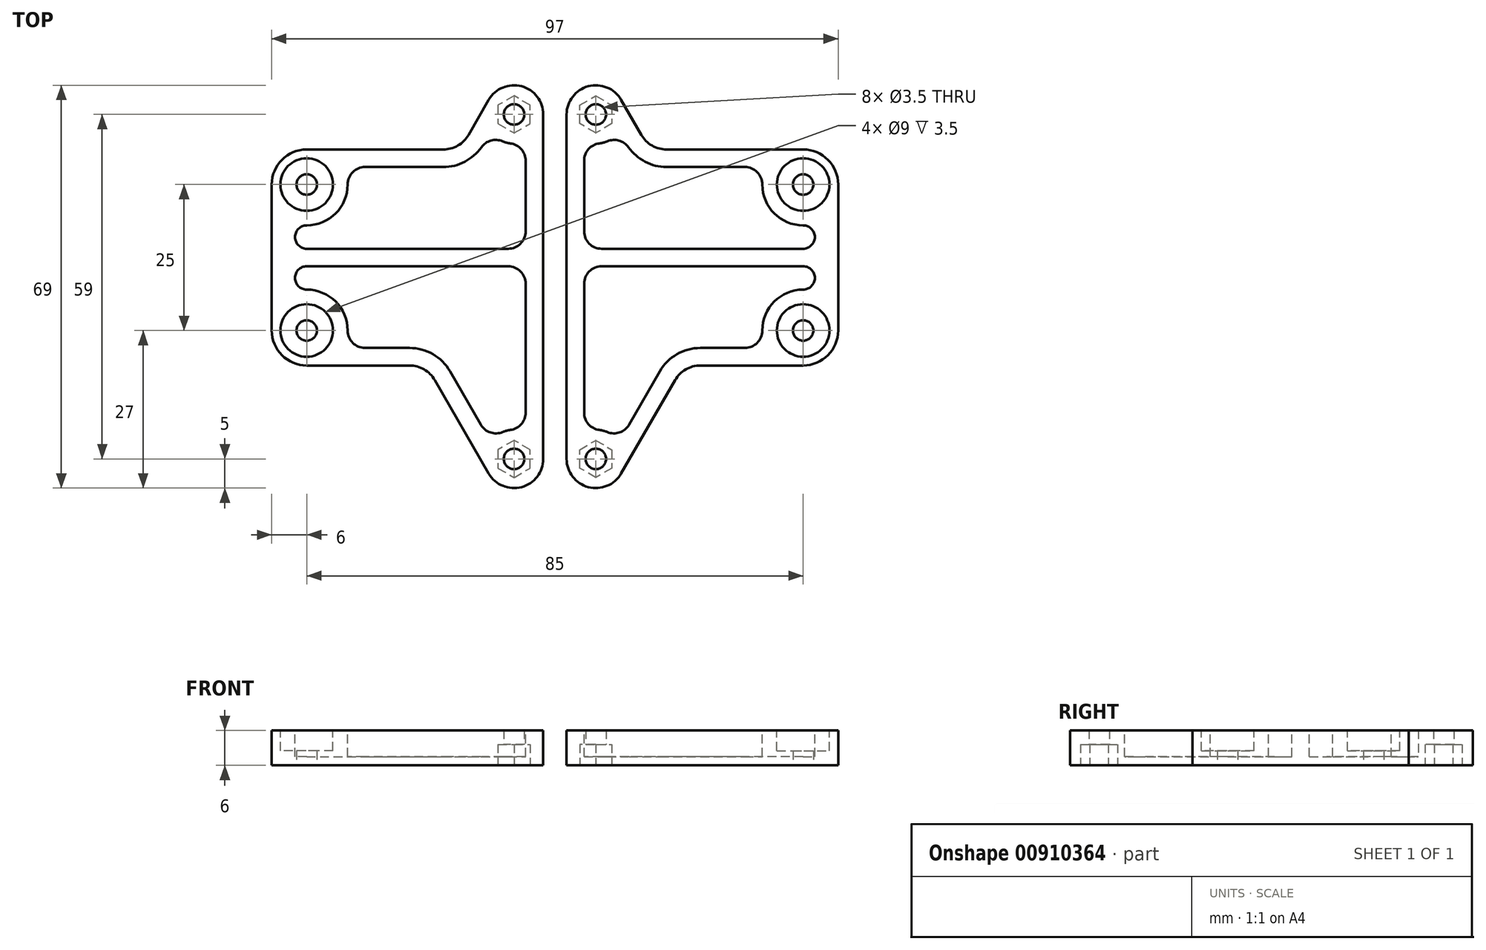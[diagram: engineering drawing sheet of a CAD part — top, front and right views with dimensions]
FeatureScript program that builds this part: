
annotation { "Feature Type Name" : "Feature", "Feature Type Description" : "" }
export const myFeature = defineFeature(function(context is Context, id is Id, definition is map)
    precondition{}
    {
        {
            var Q0;
            Q0=qCreatedBy(makeId("Top.planeOp"),FACE);
            var sketch = newSketch(context, id + "F0", { "sketchPlane" : qUnion([Q0])});
            skLineSegment(sketch, "E0", {"start": v(-42.5, 18.5) * mm, "end": v(-19.12, 18.5) * mm});
            skLineSegment(sketch, "E1", {"start": v(-2, 24.5) * mm, "end": v(-2, -34.5) * mm});
            skLineSegment(sketch, "E2", {"start": v(-24.9, -18.5) * mm, "end": v(-42.5, -18.5) * mm});
            skCircle(sketch, "E3", {"center": v(-42.5, 12.5) * mm, "radius": 1.75 * mm});
            skCircle(sketch, "E4", {"center": v(-42.5, -12.5) * mm, "radius": 1.75 * mm});
            skCircle(sketch, "E5", {"center": v(-7, 24.5) * mm, "radius": 1.75 * mm});
            skCircle(sketch, "E6", {"center": v(-7, -34.5) * mm, "radius": 1.75 * mm});
            skLineSegment(sketch, "E7", {"start": v(0, 32.5) * mm, "end": v(-48.5, 32.5) * mm, "construction": true});
            skArc(sketch, "E8", {"start": v(-2, 24.5) * mm, "mid": v(-5.7, 29.33) * mm, "end": v(-11.33, 27) * mm});
            skArc(sketch, "E9", {"start": v(-2, -34.5) * mm, "mid": v(-5.7, -39.33) * mm, "end": v(-11.33, -37) * mm});
            skLineSegment(sketch, "E10", {"start": v(-11.33, -37) * mm, "end": v(-20.57, -21) * mm});
            skLineSegment(sketch, "E11", {"start": v(-11.33, 27) * mm, "end": v(-14.8, 21) * mm});
            skArc(sketch, "E12", {"start": v(-42.5, 18.5) * mm, "mid": v(-46.74, 16.74) * mm, "end": v(-48.5, 12.5) * mm});
            skArc(sketch, "E13", {"start": v(-42.5, -18.5) * mm, "mid": v(-46.74, -16.74) * mm, "end": v(-48.5, -12.5) * mm});
            skLineSegment(sketch, "E14", {"start": v(-48.5, -12.5) * mm, "end": v(-48.5, 12.5) * mm});
            skPoint(sketch, "E15.visualSharp", {"position": v(-16.24, 18.5) * mm});
            skArc(sketch, "E15.filletArc", {"start": v(-19.12, 18.5) * mm, "mid": v(-16.62, 19.17) * mm, "end": v(-14.8, 21) * mm});
            skPoint(sketch, "E16.visualSharp", {"position": v(-22.01, -18.5) * mm});
            skArc(sketch, "E16.filletArc", {"start": v(-20.57, -21) * mm, "mid": v(-22.4, -19.17) * mm, "end": v(-24.9, -18.5) * mm});
            skLineSegment(sketch, "E17.bottom", {"start": v(-11, 28.5) * mm, "end": v(77, 28.5) * mm, "construction": true});
            skLineSegment(sketch, "E17.top", {"start": v(-11, -38.5) * mm, "end": v(77, -38.5) * mm, "construction": true});
            skLineSegment(sketch, "E17.left", {"start": v(-11, 28.5) * mm, "end": v(-11, -38.5) * mm, "construction": true});
            skLineSegment(sketch, "E17.right", {"start": v(77, 28.5) * mm, "end": v(77, -38.5) * mm, "construction": true});
            skCircle(sketch, "E18", {"center": v(-42.5, -12.5) * mm, "radius": 4 * mm, "construction": true});
            skSolve(sketch);
        }
        {
            var Q0;
            Q0 = qSketchRegion(id + "F0", true);
            extrude(context, id + "F1", {"entities" : qUnion([Q0]), "depth" : 6 * mm, "offsetDistance" : 25.4 * mm});
        }
        {
            var Q0;
            Q0=makeQuery(id+"F1.opExtrude","CAP_FACE",FACE,{"disambiguationData":[OSD([sQuery(id+"F0.wireOp",EDGE,"E0"),sQuery(id+"F0.wireOp",EDGE,"E1"),sQuery(id+"F0.wireOp",EDGE,"E2"),sQuery(id+"F0.wireOp",EDGE,"E3"),sQuery(id+"F0.wireOp",EDGE,"E4"),sQuery(id+"F0.wireOp",EDGE,"E5"),sQuery(id+"F0.wireOp",EDGE,"E6"),sQuery(id+"F0.wireOp",EDGE,"E8"),sQuery(id+"F0.wireOp",EDGE,"E9"),sQuery(id+"F0.wireOp",EDGE,"E10"),sQuery(id+"F0.wireOp",EDGE,"E11"),sQuery(id+"F0.wireOp",EDGE,"E12"),sQuery(id+"F0.wireOp",EDGE,"E13"),sQuery(id+"F0.wireOp",EDGE,"E14"),sQuery(id+"F0.wireOp",EDGE,"E15.filletArc"),sQuery(id+"F0.wireOp",EDGE,"E16.filletArc")])],"isStart":false});
            var sketch = newSketch(context, id + "F2", { "sketchPlane" : qUnion([Q0])});
            skCircle(sketch, "E19", {"center": v(-42.5, 12.5) * mm, "radius": 4.5 * mm});
            skCircle(sketch, "E20", {"center": v(-42.5, -12.5) * mm, "radius": 4.5 * mm});
            skSolve(sketch);
        }
        {
            var Q0;
            Q0 = qSketchRegion(id + "F2", true);
            var Q1;
            Q1=makeQuery(id+"F1.opExtrude","CAP_FACE",FACE,{"disambiguationData":[OSD([sQuery(id+"F0.wireOp",EDGE,"E0"),sQuery(id+"F0.wireOp",EDGE,"E1"),sQuery(id+"F0.wireOp",EDGE,"E2"),sQuery(id+"F0.wireOp",EDGE,"E3"),sQuery(id+"F0.wireOp",EDGE,"E4"),sQuery(id+"F0.wireOp",EDGE,"E5"),sQuery(id+"F0.wireOp",EDGE,"E6"),sQuery(id+"F0.wireOp",EDGE,"E8"),sQuery(id+"F0.wireOp",EDGE,"E9"),sQuery(id+"F0.wireOp",EDGE,"E10"),sQuery(id+"F0.wireOp",EDGE,"E11"),sQuery(id+"F0.wireOp",EDGE,"E12"),sQuery(id+"F0.wireOp",EDGE,"E13"),sQuery(id+"F0.wireOp",EDGE,"E14"),sQuery(id+"F0.wireOp",EDGE,"E15.filletArc"),sQuery(id+"F0.wireOp",EDGE,"E16.filletArc")])],"isStart":true});
            extrude(context, id + "F3", {"entities" : qUnion([Q0]), "operationType" : NewBodyOperationType.REMOVE, "endBound" : BoundingType.UP_TO_SURFACE, "oppositeDirection" : true, "depth" : 25.4 * mm, "endBoundEntityFace" : qUnion([Q1]), "hasOffset" : true, "offsetDistance" : 2.5 * mm});
        }
        {
            var Q0;
            Q0=makeQuery(id+"F1.opExtrude","CAP_FACE",FACE,{"disambiguationData":[OSD([sQuery(id+"F0.wireOp",EDGE,"E0"),sQuery(id+"F0.wireOp",EDGE,"E1"),sQuery(id+"F0.wireOp",EDGE,"E2"),sQuery(id+"F0.wireOp",EDGE,"E3"),sQuery(id+"F0.wireOp",EDGE,"E4"),sQuery(id+"F0.wireOp",EDGE,"E5"),sQuery(id+"F0.wireOp",EDGE,"E6"),sQuery(id+"F0.wireOp",EDGE,"E8"),sQuery(id+"F0.wireOp",EDGE,"E9"),sQuery(id+"F0.wireOp",EDGE,"E10"),sQuery(id+"F0.wireOp",EDGE,"E11"),sQuery(id+"F0.wireOp",EDGE,"E12"),sQuery(id+"F0.wireOp",EDGE,"E13"),sQuery(id+"F0.wireOp",EDGE,"E14"),sQuery(id+"F0.wireOp",EDGE,"E15.filletArc"),sQuery(id+"F0.wireOp",EDGE,"E16.filletArc")])],"isStart":true});
            var sketch = newSketch(context, id + "F4", { "sketchPlane" : qUnion([Q0])});
            skCircle(sketch, "E21.cCircle", {"center": v(-7, 34.5) * mm, "radius": 2.75 * mm, "construction": true});
            skLineSegment(sketch, "E21.0", {"start": v(-4.25, 36.09) * mm, "end": v(-4.25, 32.91) * mm});
            skLineSegment(sketch, "E21.1", {"start": v(-4.25, 32.91) * mm, "end": v(-7, 31.32) * mm});
            skLineSegment(sketch, "E21.2", {"start": v(-7, 31.32) * mm, "end": v(-9.75, 32.91) * mm});
            skLineSegment(sketch, "E21.3", {"start": v(-9.75, 32.91) * mm, "end": v(-9.75, 36.09) * mm});
            skLineSegment(sketch, "E21.4", {"start": v(-9.75, 36.09) * mm, "end": v(-7, 37.68) * mm});
            skLineSegment(sketch, "E21.5", {"start": v(-7, 37.68) * mm, "end": v(-4.25, 36.09) * mm});
            skPoint(sketch, "E21.0.midPoint", {"position": v(-4.25, 34.5) * mm});
            skCircle(sketch, "E22.cCircle", {"center": v(-7, -24.5) * mm, "radius": 2.75 * mm, "construction": true});
            skLineSegment(sketch, "E22.0", {"start": v(-7, -21.32) * mm, "end": v(-4.25, -22.91) * mm});
            skLineSegment(sketch, "E22.1", {"start": v(-4.25, -22.91) * mm, "end": v(-4.25, -26.09) * mm});
            skLineSegment(sketch, "E22.2", {"start": v(-4.25, -26.09) * mm, "end": v(-7, -27.68) * mm});
            skLineSegment(sketch, "E22.3", {"start": v(-7, -27.68) * mm, "end": v(-9.75, -26.09) * mm});
            skLineSegment(sketch, "E22.4", {"start": v(-9.75, -26.09) * mm, "end": v(-9.75, -22.91) * mm});
            skLineSegment(sketch, "E22.5", {"start": v(-9.75, -22.91) * mm, "end": v(-7, -21.32) * mm});
            skPoint(sketch, "E22.0.midPoint", {"position": v(-5.63, -22.12) * mm});
            skSolve(sketch);
        }
        {
            var Q0;
            Q0 = qSketchRegion(id + "F4", true);
            var Q1;
            Q1=makeQuery(id+"F1.opExtrude","CAP_FACE",FACE,{"disambiguationData":[OSD([sQuery(id+"F0.wireOp",EDGE,"E0"),sQuery(id+"F0.wireOp",EDGE,"E1"),sQuery(id+"F0.wireOp",EDGE,"E2"),sQuery(id+"F0.wireOp",EDGE,"E3"),sQuery(id+"F0.wireOp",EDGE,"E4"),sQuery(id+"F0.wireOp",EDGE,"E5"),sQuery(id+"F0.wireOp",EDGE,"E6"),sQuery(id+"F0.wireOp",EDGE,"E8"),sQuery(id+"F0.wireOp",EDGE,"E9"),sQuery(id+"F0.wireOp",EDGE,"E10"),sQuery(id+"F0.wireOp",EDGE,"E11"),sQuery(id+"F0.wireOp",EDGE,"E12"),sQuery(id+"F0.wireOp",EDGE,"E13"),sQuery(id+"F0.wireOp",EDGE,"E14"),sQuery(id+"F0.wireOp",EDGE,"E15.filletArc"),sQuery(id+"F0.wireOp",EDGE,"E16.filletArc")])],"isStart":false});
            extrude(context, id + "F5", {"entities" : qUnion([Q0]), "operationType" : NewBodyOperationType.REMOVE, "endBound" : BoundingType.UP_TO_SURFACE, "oppositeDirection" : true, "depth" : 25.4 * mm, "endBoundEntityFace" : qUnion([Q1]), "hasOffset" : true, "offsetDistance" : 2.4 * mm});
        }
        {
            var Q0;
            Q0=makeQuery(id+"F1.opExtrude","CAP_FACE",FACE,{"disambiguationData":[OSD([sQuery(id+"F0.wireOp",EDGE,"E0"),sQuery(id+"F0.wireOp",EDGE,"E1"),sQuery(id+"F0.wireOp",EDGE,"E2"),sQuery(id+"F0.wireOp",EDGE,"E3"),sQuery(id+"F0.wireOp",EDGE,"E4"),sQuery(id+"F0.wireOp",EDGE,"E5"),sQuery(id+"F0.wireOp",EDGE,"E6"),sQuery(id+"F0.wireOp",EDGE,"E8"),sQuery(id+"F0.wireOp",EDGE,"E9"),sQuery(id+"F0.wireOp",EDGE,"E10"),sQuery(id+"F0.wireOp",EDGE,"E11"),sQuery(id+"F0.wireOp",EDGE,"E12"),sQuery(id+"F0.wireOp",EDGE,"E13"),sQuery(id+"F0.wireOp",EDGE,"E14"),sQuery(id+"F0.wireOp",EDGE,"E15.filletArc"),sQuery(id+"F0.wireOp",EDGE,"E16.filletArc")])],"isStart":false});
            var sketch = newSketch(context, id + "F6", { "sketchPlane" : qUnion([Q0])});
            skArc(sketch, "E23.0", {"start": v(-24.9, -15.5) * mm, "mid": v(-20.9, -16.57) * mm, "end": v(-17.97, -19.5) * mm});
            skLineSegment(sketch, "E23.1", {"start": v(-36.18, -15.5) * mm, "end": v(-24.9, -15.5) * mm});
            skLineSegment(sketch, "E23.2", {"start": v(-17.97, -19.5) * mm, "end": v(-11.02, -31.53) * mm});
            skLineSegment(sketch, "E23.4", {"start": v(-5, -29.92) * mm, "end": v(-5, -1.5) * mm});
            skLineSegment(sketch, "E23.5", {"start": v(-11.02, 21.53) * mm, "end": v(-12.2, 19.5) * mm});
            skArc(sketch, "E23.6", {"start": v(-12.2, 19.5) * mm, "mid": v(-15.12, 16.57) * mm, "end": v(-19.12, 15.5) * mm});
            skLineSegment(sketch, "E23.7", {"start": v(-19.12, 15.5) * mm, "end": v(-36.18, 15.5) * mm});
            skArc(sketch, "E24", {"start": v(-36.18, -15.5) * mm, "mid": v(-36.58, -8.76) * mm, "end": v(-42.5, -5.5) * mm});
            skArc(sketch, "E25", {"start": v(-42.5, 5.5) * mm, "mid": v(-36.58, 8.76) * mm, "end": v(-36.18, 15.5) * mm});
            skArc(sketch, "E26", {"start": v(-5, 19.92) * mm, "mid": v(-8.3, 19.67) * mm, "end": v(-11.02, 21.53) * mm});
            skArc(sketch, "E27", {"start": v(-5, -29.92) * mm, "mid": v(-8.3, -29.67) * mm, "end": v(-11.02, -31.53) * mm});
            skLineSegment(sketch, "E28", {"start": v(-5, 1.5) * mm, "end": v(-42.5, 1.5) * mm});
            skPoint(sketch, "E28.endSnap0", {"position": v(-42.5, 0) * mm});
            skLineSegment(sketch, "E29", {"start": v(-5, -1.5) * mm, "end": v(-42.5, -1.5) * mm});
            skLineSegment(sketch, "E30.trimOffspring", {"start": v(-5, 1.5) * mm, "end": v(-5, 19.92) * mm});
            skArc(sketch, "E31", {"start": v(-42.5, 5.5) * mm, "mid": v(-44.5, 3.5) * mm, "end": v(-42.5, 1.5) * mm});
            skArc(sketch, "E32", {"start": v(-42.5, -5.5) * mm, "mid": v(-44.5, -3.5) * mm, "end": v(-42.5, -1.5) * mm});
            skSolve(sketch);
        }
        {
            var Q0;
            Q0 = qSketchRegion(id + "F6", true);
            var Q1;
            Q1=makeQuery(id+"F1.opExtrude","CAP_FACE",FACE,{"disambiguationData":[OSD([sQuery(id+"F0.wireOp",EDGE,"E0"),sQuery(id+"F0.wireOp",EDGE,"E1"),sQuery(id+"F0.wireOp",EDGE,"E2"),sQuery(id+"F0.wireOp",EDGE,"E3"),sQuery(id+"F0.wireOp",EDGE,"E4"),sQuery(id+"F0.wireOp",EDGE,"E5"),sQuery(id+"F0.wireOp",EDGE,"E6"),sQuery(id+"F0.wireOp",EDGE,"E8"),sQuery(id+"F0.wireOp",EDGE,"E9"),sQuery(id+"F0.wireOp",EDGE,"E10"),sQuery(id+"F0.wireOp",EDGE,"E11"),sQuery(id+"F0.wireOp",EDGE,"E12"),sQuery(id+"F0.wireOp",EDGE,"E13"),sQuery(id+"F0.wireOp",EDGE,"E14"),sQuery(id+"F0.wireOp",EDGE,"E15.filletArc"),sQuery(id+"F0.wireOp",EDGE,"E16.filletArc")])],"isStart":true});
            extrude(context, id + "F7", {"entities" : qUnion([Q0]), "operationType" : NewBodyOperationType.REMOVE, "endBound" : BoundingType.UP_TO_SURFACE, "oppositeDirection" : true, "depth" : 25.4 * mm, "endBoundEntityFace" : qUnion([Q1]), "hasOffset" : true, "offsetDistance" : 1.5 * mm});
        }
        {
            var Q0;
            Q0=makeQuery(id+"F7.boolean.opBoolean","COPY",EDGE,{"derivedFrom":makeQuery(id+"F7.opExtrude","SWEPT_EDGE",EDGE,{"disambiguationData":[OSD([sQuery(id+"F6.wireOp",EDGE,"E23.7"),sQuery(id+"F6.wireOp",EDGE,"E25")])]})});
            var Q1;
            Q1=makeQuery(id+"F7.boolean.opBoolean","COPY",EDGE,{"derivedFrom":makeQuery(id+"F7.opExtrude","SWEPT_EDGE",EDGE,{"disambiguationData":[OSD([sQuery(id+"F6.wireOp",EDGE,"E23.5"),sQuery(id+"F6.wireOp",EDGE,"E26")])]})});
            var Q2;
            Q2=makeQuery(id+"F7.boolean.opBoolean","COPY",EDGE,{"derivedFrom":makeQuery(id+"F7.opExtrude","SWEPT_EDGE",EDGE,{"disambiguationData":[OSD([sQuery(id+"F6.wireOp",EDGE,"E26"),sQuery(id+"F6.wireOp",EDGE,"E30.trimOffspring")])]})});
            var Q3;
            Q3=makeQuery(id+"F7.boolean.opBoolean","COPY",EDGE,{"derivedFrom":makeQuery(id+"F7.opExtrude","SWEPT_EDGE",EDGE,{"disambiguationData":[OSD([sQuery(id+"F6.wireOp",EDGE,"E28"),sQuery(id+"F6.wireOp",EDGE,"E30.trimOffspring")])]})});
            var Q4;
            Q4=makeQuery(id+"F7.boolean.opBoolean","COPY",EDGE,{"derivedFrom":makeQuery(id+"F7.opExtrude","SWEPT_EDGE",EDGE,{"disambiguationData":[OSD([sQuery(id+"F6.wireOp",EDGE,"E23.4"),sQuery(id+"F6.wireOp",EDGE,"E29")])]})});
            var Q5;
            Q5=makeQuery(id+"F7.boolean.opBoolean","COPY",EDGE,{"derivedFrom":makeQuery(id+"F7.opExtrude","SWEPT_EDGE",EDGE,{"disambiguationData":[OSD([sQuery(id+"F6.wireOp",EDGE,"E23.2"),sQuery(id+"F6.wireOp",EDGE,"E27")])]})});
            var Q6;
            Q6=makeQuery(id+"F7.boolean.opBoolean","COPY",EDGE,{"derivedFrom":makeQuery(id+"F7.opExtrude","SWEPT_EDGE",EDGE,{"disambiguationData":[OSD([sQuery(id+"F6.wireOp",EDGE,"E23.4"),sQuery(id+"F6.wireOp",EDGE,"E27")])]})});
            var Q7;
            Q7=makeQuery(id+"F7.boolean.opBoolean","COPY",EDGE,{"derivedFrom":makeQuery(id+"F7.opExtrude","SWEPT_EDGE",EDGE,{"disambiguationData":[OSD([sQuery(id+"F6.wireOp",EDGE,"E23.1"),sQuery(id+"F6.wireOp",EDGE,"E24")])]})});
            fillet(context, id + "F8", {"entities" : qUnion([Q0, Q1, Q2, Q3, Q4, Q5, Q6, Q7]), "radius" : 3 * mm, "tangentPropagation" : true, "allowEdgeOverflow" : false});
        }
        {
            var Q0;
            Q0=makeQuery(id+"F1.opExtrude","SWEPT_BODY",BODY,{"disambiguationData":[OSD([sQuery(id+"F0.wireOp",EDGE,"E0"),sQuery(id+"F0.wireOp",EDGE,"E1"),sQuery(id+"F0.wireOp",EDGE,"E2"),sQuery(id+"F0.wireOp",EDGE,"E3"),sQuery(id+"F0.wireOp",EDGE,"E4"),sQuery(id+"F0.wireOp",EDGE,"E5"),sQuery(id+"F0.wireOp",EDGE,"E6"),sQuery(id+"F0.wireOp",EDGE,"E8"),sQuery(id+"F0.wireOp",EDGE,"E9"),sQuery(id+"F0.wireOp",EDGE,"E10"),sQuery(id+"F0.wireOp",EDGE,"E11"),sQuery(id+"F0.wireOp",EDGE,"E12"),sQuery(id+"F0.wireOp",EDGE,"E13"),sQuery(id+"F0.wireOp",EDGE,"E14"),sQuery(id+"F0.wireOp",EDGE,"E15.filletArc"),sQuery(id+"F0.wireOp",EDGE,"E16.filletArc")])]});
            var Q1;
            Q1=qCreatedBy(makeId("Right.planeOp"),FACE);
            mirror(context, id + "F9", {"operationType" : NewBodyOperationType.ADD, "entities" : qUnion([Q0]), "mirrorPlane" : qUnion([Q1])});
        }
    });
